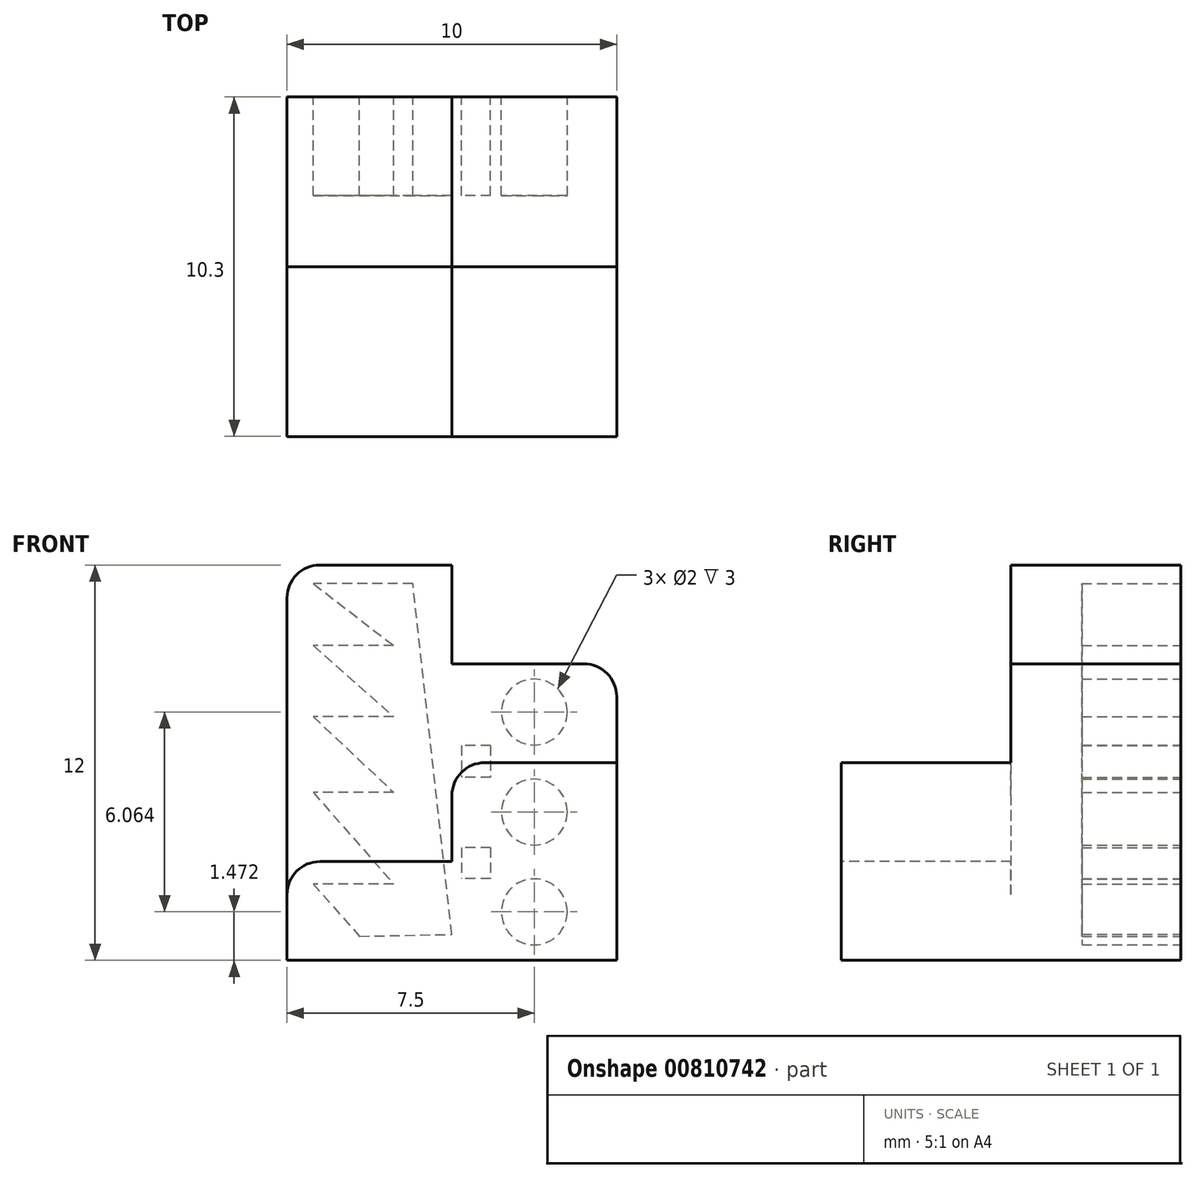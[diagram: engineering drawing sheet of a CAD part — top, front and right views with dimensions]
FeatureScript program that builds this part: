
annotation { "Feature Type Name" : "Feature", "Feature Type Description" : "" }
export const myFeature = defineFeature(function(context is Context, id is Id, definition is map)
    precondition{}
    {
        {
            var Q0;
            Q0=qCreatedBy(makeId("Top.planeOp"),FACE);
            var sketch = newSketch(context, id + "F0", { "sketchPlane" : qUnion([Q0])});
            skLineSegment(sketch, "E0.bottom", {"start": v(5, 5.15) * mm, "end": v(-5, 5.15) * mm});
            skLineSegment(sketch, "E0.top", {"start": v(5, -5.15) * mm, "end": v(-5, -5.15) * mm});
            skLineSegment(sketch, "E0.left", {"start": v(5, 5.15) * mm, "end": v(5, -5.15) * mm});
            skLineSegment(sketch, "E0.right", {"start": v(-5, 5.15) * mm, "end": v(-5, -5.15) * mm});
            skPoint(sketch, "E0.middle", {"position": v(0, 0) * mm});
            skSolve(sketch);
        }
        {
            var Q0;
            Q0 = qSketchRegion(id + "F0", true);
            extrude(context, id + "F1", {"entities" : qUnion([Q0]), "depth" : 3 * mm, "offsetDistance" : 25 * mm});
        }
        {
            var Q0;
            Q0=makeQuery(id+"F1.opExtrude","CAP_FACE",FACE,{"disambiguationData":[OSD([sQuery(id+"F0.wireOp",EDGE,"E0.bottom"),sQuery(id+"F0.wireOp",EDGE,"E0.top"),sQuery(id+"F0.wireOp",EDGE,"E0.left"),sQuery(id+"F0.wireOp",EDGE,"E0.right")])],"isStart":false});
            var sketch = newSketch(context, id + "F2", { "sketchPlane" : qUnion([Q0])});
            skLineSegment(sketch, "E1", {"start": v(-5, 0) * mm, "end": v(0, 0) * mm});
            skLineSegment(sketch, "E2", {"start": v(0, 0) * mm, "end": v(0, -5.15) * mm});
            skLineSegment(sketch, "E3.bottom", {"start": v(5, 5.15) * mm, "end": v(-2.5, 5.15) * mm});
            skLineSegment(sketch, "E3.top", {"start": v(5, -5.15) * mm, "end": v(0, -5.15) * mm});
            skLineSegment(sketch, "E3.left", {"start": v(5, 5.15) * mm, "end": v(5, -5.15) * mm});
            skLineSegment(sketch, "E4", {"start": v(-5, -5.15) * mm, "end": v(-5, 5.15) * mm});
            skLineSegment(sketch, "E5", {"start": v(5, -5.15) * mm, "end": v(5, 5.15) * mm});
            skLineSegment(sketch, "E6", {"start": v(-5, 5.15) * mm, "end": v(5, 5.15) * mm});
            skSolve(sketch);
        }
        {
            var Q0;
            {var subQ5=sQuery(id+"F2.wireOp",EDGE,"E1");Q0=makeQuery(id+"F2.imprint","IMPRINT",FACE,{"disambiguationData":[TD([[makeQuery(id+"F2.imprint","IMPRINT",EDGE,{"derivedFrom":subQ5}),1.0]])]});}
            extrude(context, id + "F3", {"entities" : qUnion([Q0]), "operationType" : NewBodyOperationType.ADD, "depth" : 3 * mm, "offsetDistance" : 25 * mm});
        }
        {
            var Q0;
            Q0=makeQuery(id+"F3.opExtrude","CAP_FACE",FACE,{"disambiguationData":[OSD([sQuery(id+"F0.wireOp",EDGE,"E0.top"),sQuery(id+"F2.wireOp",EDGE,"E1"),sQuery(id+"F2.wireOp",EDGE,"E2"),sQuery(id+"F2.wireOp",EDGE,"E4"),sQuery(id+"F2.wireOp",EDGE,"E5"),sQuery(id+"F2.wireOp",EDGE,"E6")])],"isStart":false});
            var sketch = newSketch(context, id + "F4", { "sketchPlane" : qUnion([Q0])});
            skLineSegment(sketch, "E7.bottom", {"start": v(-5, 0) * mm, "end": v(5, 0) * mm});
            skLineSegment(sketch, "E7.top", {"start": v(-5, 5.15) * mm, "end": v(5, 5.15) * mm});
            skLineSegment(sketch, "E7.left", {"start": v(-5, 0) * mm, "end": v(-5, 5.15) * mm});
            skLineSegment(sketch, "E7.right", {"start": v(5, 0) * mm, "end": v(5, 5.15) * mm});
            skSolve(sketch);
        }
        {
            var Q0;
            Q0 = qSketchRegion(id + "F4", true);
            extrude(context, id + "F5", {"entities" : qUnion([Q0]), "operationType" : NewBodyOperationType.ADD, "depth" : 3 * mm, "offsetDistance" : 25 * mm});
        }
        {
            var Q0;
            Q0=makeQuery(id+"F5.opExtrude","CAP_FACE",FACE,{"disambiguationData":[OSD([sQuery(id+"F4.wireOp",EDGE,"E7.bottom"),sQuery(id+"F4.wireOp",EDGE,"E7.top"),sQuery(id+"F4.wireOp",EDGE,"E7.left"),sQuery(id+"F4.wireOp",EDGE,"E7.right")])],"isStart":false});
            var sketch = newSketch(context, id + "F6", { "sketchPlane" : qUnion([Q0])});
            skLineSegment(sketch, "E8.bottom", {"start": v(0, 0) * mm, "end": v(-5, 0) * mm});
            skLineSegment(sketch, "E8.top", {"start": v(0, 5.15) * mm, "end": v(-5, 5.15) * mm});
            skLineSegment(sketch, "E8.left", {"start": v(0, 0) * mm, "end": v(0, 5.15) * mm});
            skLineSegment(sketch, "E8.right", {"start": v(-5, 0) * mm, "end": v(-5, 5.15) * mm});
            skSolve(sketch);
        }
        {
            var Q0;
            Q0=makeQuery(id+"F6.imprint","IMPRINT",FACE,{"disambiguationData":[TD([[makeQuery(id+"F6.imprint","IMPRINT",EDGE,{"derivedFrom":sQuery(id+"F6.wireOp",EDGE,"E8.bottom")}),1.0]])]});
            extrude(context, id + "F7", {"entities" : qUnion([Q0]), "operationType" : NewBodyOperationType.ADD, "depth" : 3 * mm, "offsetDistance" : 25 * mm});
        }
        {
            var Q0;
            Q0=makeQuery(id+"F7.boolean.opBoolean","MERGE",FACE,{"derivedFrom":[makeQuery(id+"F5.boolean.opBoolean","MERGE",FACE,{"derivedFrom":[makeQuery(id+"F3.boolean.opBoolean","MERGE",FACE,{"derivedFrom":[makeQuery(id+"F1.opExtrude","SWEPT_FACE",FACE,{"disambiguationData":[OSD([sQuery(id+"F0.wireOp",EDGE,"E0.bottom")])]}),makeQuery(id+"F3.opExtrude","SWEPT_FACE",FACE,{"disambiguationData":[OSD([sQuery(id+"F2.wireOp",EDGE,"E6")])]})]}),makeQuery(id+"F5.opExtrude","SWEPT_FACE",FACE,{"disambiguationData":[OSD([sQuery(id+"F4.wireOp",EDGE,"E7.top")])]})]}),makeQuery(id+"F7.opExtrude","SWEPT_FACE",FACE,{"disambiguationData":[OSD([sQuery(id+"F6.wireOp",EDGE,"E8.top")])]})]});
            var sketch = newSketch(context, id + "F8", { "sketchPlane" : qUnion([Q0])});
            skLineSegment(sketch, "E9", {"start": v(-2.5, 9) * mm, "end": v(-2.5, 0) * mm, "construction": true});
            skCircle(sketch, "E10", {"center": v(-2.5, 7.54) * mm, "radius": 1 * mm});
            skCircle(sketch, "E11", {"center": v(-2.5, 4.5) * mm, "radius": 1 * mm});
            skCircle(sketch, "E12", {"center": v(-2.5, 1.47) * mm, "radius": 1 * mm});
            skLineSegment(sketch, "E13", {"start": v(0, 0.79) * mm, "end": v(1.19, 11.43) * mm});
            skLineSegment(sketch, "E14", {"start": v(1.19, 11.43) * mm, "end": v(4.2, 11.43) * mm});
            skLineSegment(sketch, "E15", {"start": v(4.2, 11.43) * mm, "end": v(1.77, 9.56) * mm});
            skLineSegment(sketch, "E16", {"start": v(1.77, 9.56) * mm, "end": v(4.2, 9.56) * mm});
            skLineSegment(sketch, "E17", {"start": v(4.2, 9.56) * mm, "end": v(1.77, 7.4) * mm});
            skLineSegment(sketch, "E18", {"start": v(1.77, 7.4) * mm, "end": v(4.2, 7.4) * mm});
            skLineSegment(sketch, "E19", {"start": v(4.2, 7.4) * mm, "end": v(1.77, 5.1) * mm});
            skLineSegment(sketch, "E20", {"start": v(1.77, 5.1) * mm, "end": v(4.2, 5.1) * mm});
            skLineSegment(sketch, "E21", {"start": v(4.2, 5.1) * mm, "end": v(1.77, 2.32) * mm});
            skLineSegment(sketch, "E22", {"start": v(1.77, 2.32) * mm, "end": v(4.2, 2.32) * mm});
            skLineSegment(sketch, "E23", {"start": v(4.2, 2.32) * mm, "end": v(2.8, 0.73) * mm});
            skLineSegment(sketch, "E24", {"start": v(2.8, 0.73) * mm, "end": v(0, 0.79) * mm});
            skLineSegment(sketch, "E25.bottom", {"start": v(-1.17, 3.42) * mm, "end": v(-0.3, 3.42) * mm});
            skLineSegment(sketch, "E25.top", {"start": v(-1.17, 2.49) * mm, "end": v(-0.3, 2.49) * mm});
            skLineSegment(sketch, "E25.left", {"start": v(-1.17, 3.42) * mm, "end": v(-1.17, 2.49) * mm});
            skLineSegment(sketch, "E25.right", {"start": v(-0.3, 3.42) * mm, "end": v(-0.3, 2.49) * mm});
            skLineSegment(sketch, "E26.bottom", {"start": v(-1.17, 6.52) * mm, "end": v(-0.3, 6.52) * mm});
            skLineSegment(sketch, "E26.top", {"start": v(-1.17, 5.56) * mm, "end": v(-0.3, 5.56) * mm});
            skLineSegment(sketch, "E26.left", {"start": v(-1.17, 6.52) * mm, "end": v(-1.17, 5.56) * mm});
            skLineSegment(sketch, "E26.right", {"start": v(-0.3, 6.52) * mm, "end": v(-0.3, 5.56) * mm});
            skSolve(sketch);
        }
        {
            var Q0;
            Q0=makeQuery(id+"F8.imprint","IMPRINT",FACE,{"disambiguationData":[TD([[makeQuery(id+"F8.imprint","IMPRINT",EDGE,{"derivedFrom":sQuery(id+"F8.wireOp",EDGE,"E10")}),1.0]])]});
            var Q1;
            Q1=makeQuery(id+"F8.imprint","IMPRINT",FACE,{"disambiguationData":[TD([[makeQuery(id+"F8.imprint","IMPRINT",EDGE,{"derivedFrom":sQuery(id+"F8.wireOp",EDGE,"E11")}),1.0]])]});
            var Q2;
            Q2=makeQuery(id+"F8.imprint","IMPRINT",FACE,{"disambiguationData":[TD([[makeQuery(id+"F8.imprint","IMPRINT",EDGE,{"derivedFrom":sQuery(id+"F8.wireOp",EDGE,"E12")}),1.0]])]});
            var Q3;
            Q3=makeQuery(id+"F8.imprint","IMPRINT",FACE,{"disambiguationData":[TD([[makeQuery(id+"F8.imprint","IMPRINT",EDGE,{"derivedFrom":sQuery(id+"F8.wireOp",EDGE,"E25.bottom")}),-1.0]])]});
            var Q4;
            Q4=makeQuery(id+"F8.imprint","IMPRINT",FACE,{"disambiguationData":[TD([[makeQuery(id+"F8.imprint","IMPRINT",EDGE,{"derivedFrom":sQuery(id+"F8.wireOp",EDGE,"E26.bottom")}),-1.0]])]});
            var Q5;
            Q5=makeQuery(id+"F8.imprint","IMPRINT",FACE,{"disambiguationData":[TD([[makeQuery(id+"F8.imprint","IMPRINT",EDGE,{"derivedFrom":sQuery(id+"F8.wireOp",EDGE,"E13")}),-1.0]])]});
            extrude(context, id + "F9", {"entities" : qUnion([Q0, Q1, Q2, Q3, Q4, Q5]), "operationType" : NewBodyOperationType.REMOVE, "oppositeDirection" : true, "depth" : 3 * mm, "offsetDistance" : 25 * mm});
        }
        {
            var Q0;
            Q0=makeQuery(id+"F7.opExtrude","CAP_EDGE",EDGE,{"disambiguationData":[OSD([sQuery(id+"F6.wireOp",EDGE,"E8.right")])],"isStart":false});
            var Q1;
            Q1=makeQuery(id+"F5.opExtrude","CAP_EDGE",EDGE,{"disambiguationData":[OSD([sQuery(id+"F4.wireOp",EDGE,"E7.right")])],"isStart":false});
            var Q2;
            Q2=makeQuery(id+"F3.opExtrude","CAP_EDGE",EDGE,{"disambiguationData":[OSD([sQuery(id+"F2.wireOp",EDGE,"E2")])],"isStart":false});
            var Q3;
            Q3=makeQuery(id+"F1.opExtrude","CAP_EDGE",EDGE,{"disambiguationData":[OSD([sQuery(id+"F0.wireOp",EDGE,"E0.right")])],"isStart":false});
            fillet(context, id + "F10", {"entities" : qUnion([Q0, Q1, Q2, Q3]), "radius" : 1 * mm, "tangentPropagation" : true, "allowEdgeOverflow" : false});
        }
    });
